# Revit family: spectral_iris_iris-w-d-led_1950-830-t
name_source: partatom
category: Lighting Fixtures
revit_build: Autodesk Revit 2016 (Build: 20150220_1215(x64)
units: mm (PartAtom-declared; Revit-internal decimal feet)

## family parameters
Cut with Voids When Loaded = No
Host = Face
Light Source = No
Part Type = Normal
Room Calculation Point = No
Round Connector Dimension = Use Diameter
Shared = No

## types (1)
- SPECTRAL IRIS (1 x )
    Apparent Load = 0 VA
    Approval mark = CE
    CIE Flux Codes = 69 93 99 100 100
    Control Gear = Electronic transformer
    Default Elevation = 1800 mm
    Description = SPI0000052AY
Surface-mounted wall luminaire IRIS

Design:
Direct beam ring-shaped luminaire made of highly transparent plastic. The rotationally symmetrical, flame retardant and impact resistant luminaire housing is slightly offset from the wall. Glare reduction by means of round diffuser panel made of highly transparent plastic with microprism structure which clips in from the front. Central round white powder-coated steel panel to cover the gear tray and for wall mounting. All metal parts are powder coated. Wall luminaire with heat-resistant wiring. 

Colour: housing – transparent; ceiling box similar to RAL 9016 White silk matt. Colour accentuation of the housing possible by inserting a separately available colour inlay film. 

LED: 3 LED ring segment boards for indirect lighting component.
Safety class I, Protection rating IP20
    Height = 50 mm
    Lamp = 1 x
    Lamp count = 1
    Length = 410 mm
    Luminous efficacy = 0 lm/W
    Manufacturer = Ridi
    ModVariant = No
    Model = IRIS-W-D-LED 1950-830-T
    Mounting Place = Wall
    Mounting Type = Surface mounted
    Number of Poles = 1
    OnlyDefault = Yes
    Power Factor = 1
    Product Name = SPECTRAL IRIS
    Product group = Wall-mounted luminaire
    ProductGroupID = 20
    Protection Class = Protection class
    Protection Degree = IP 20
    RlxData = <blob elided: 45961 chars, md5=977c099e>
    Socket = socket
    Standby Power = 0 W
    System Light Flux = 0 lm
    System Power = 0 W
    Type Image = 001_iri_wab_01_01700246_001.jpg
    URL = http://reluxnet.relux.com
    VarID = 1
    Voltage = 0 V
    Weight = 0.00 kg
    Width = 0 mm  [stored 0 ft]

note: [stored X ft] marks values corroborated as IEEE doubles in the binary element streams (Revit-internal decimal feet)

## geometry (parser evidence)
native form markers: Blend x4, Sweep x10
no freeform markers — native parametric forms only
